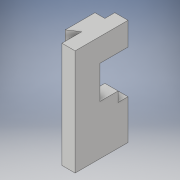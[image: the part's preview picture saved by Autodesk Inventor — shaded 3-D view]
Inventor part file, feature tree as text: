
AUTODESK INVENTOR PART (.ipt)
format: ipt  version: 2019 (Build 230136000, 136)  size: 131,072 bytes
history: native  units: mm
features: extrude x3, sketch x3, projected_geometry x2
ambient origin geometry x8: Origin, YZ Plane, XZ Plane, XY Plane, X Axis, Y Axis, Z Axis, Center Point
bodies: Solid1 (feature_tree)
feature tree (8):
  extrude  "Extrusion1"  Depth=4.0mm
  extrude  "Extrusion2"  Depth=3.0mm
  extrude  "Extrusion3"  Depth=4.0mm
  sketch  "Sketch1"  dims[d0=16.0mm d1=4.0mm]
  sketch  "Sketch2"  dims[d2=6.0mm d3=3.0mm]
  projected_geometry  "Projected Loop1"
  sketch  "Sketch3"  dims[d4=3.0mm d5=9.0mm d6=32.0mm d7=0.0mm d8=25.0mm d9=5.5mm d10=3.0mm d11=0.0mm d12=12.0mm d13=3.0mm d14=3.0mm d15=4.0mm d16=0.0mm]
  projected_geometry  "Projected Loop2"
